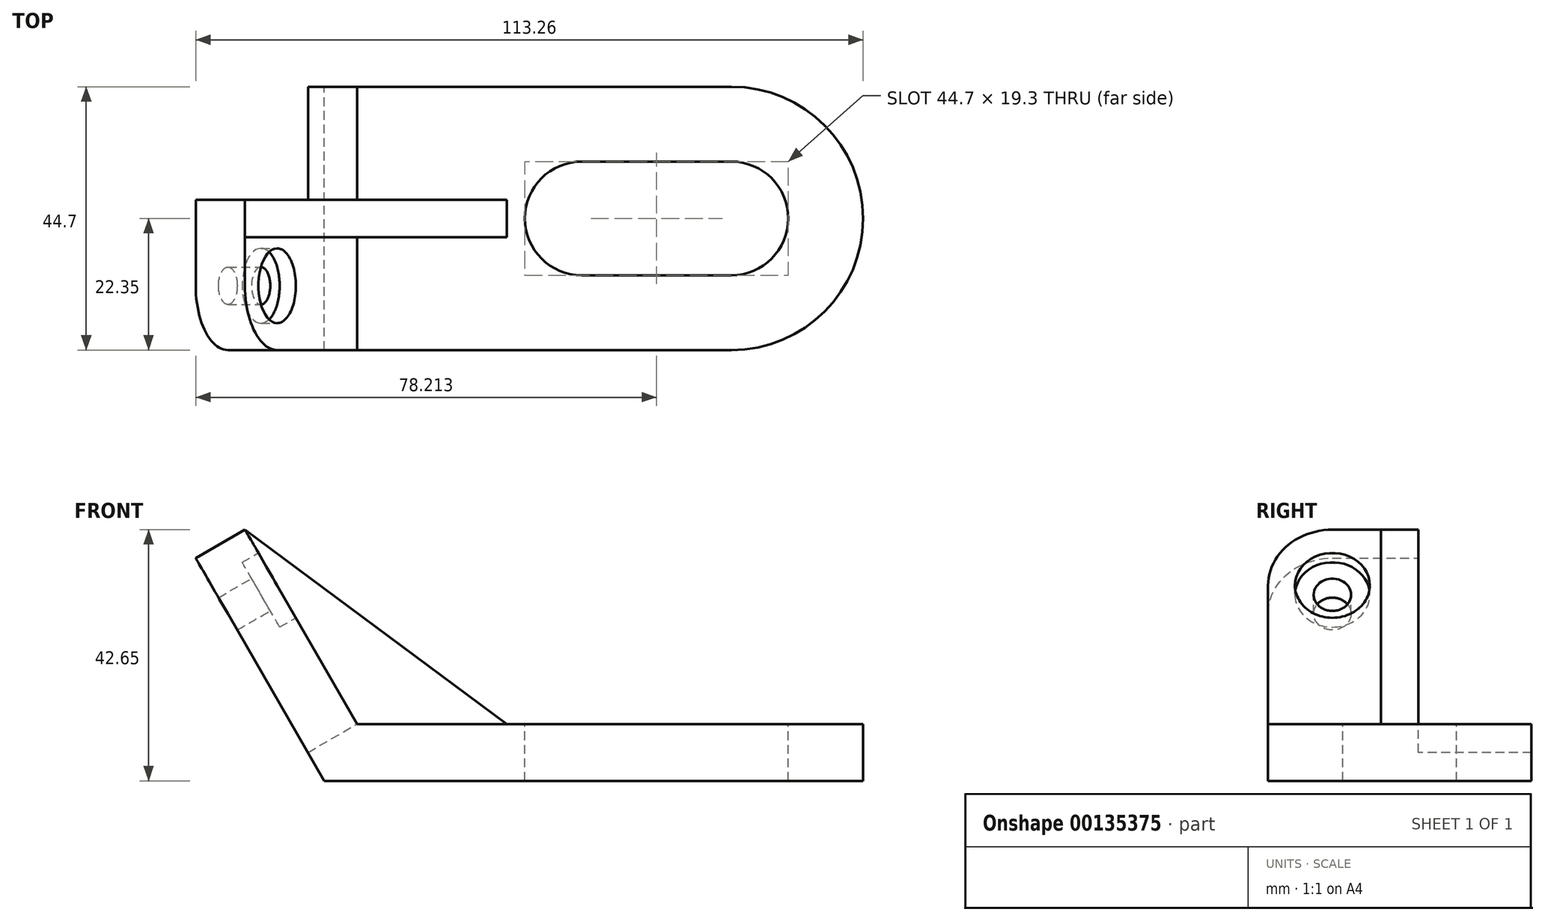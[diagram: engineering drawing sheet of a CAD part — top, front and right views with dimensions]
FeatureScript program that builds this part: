
annotation { "Feature Type Name" : "Feature", "Feature Type Description" : "" }
export const myFeature = defineFeature(function(context is Context, id is Id, definition is map)
    precondition{}
    {
        {
            var Q0;
            Q0=qCreatedBy(makeId("Front.planeOp"),FACE);
            var sketch = newSketch(context, id + "F0", { "sketchPlane" : qUnion([Q0])});
            skLineSegment(sketch, "E0", {"start": v(91.42, 9.65) * mm, "end": v(5.57, 9.65) * mm});
            skLineSegment(sketch, "E1", {"start": v(91.42, 9.65) * mm, "end": v(91.42, 0) * mm});
            skLineSegment(sketch, "E2", {"start": v(91.42, 0) * mm, "end": v(0, 0) * mm});
            skLineSegment(sketch, "E3", {"start": v(0, 0) * mm, "end": v(-21.84, 37.82) * mm});
            skLineSegment(sketch, "E4", {"start": v(-21.84, 37.82) * mm, "end": v(-13.48, 42.65) * mm});
            skLineSegment(sketch, "E5", {"start": v(-13.48, 42.65) * mm, "end": v(5.57, 9.65) * mm});
            skLineSegment(sketch, "E6", {"start": v(-13.48, 42.65) * mm, "end": v(30.97, 9.65) * mm});
            skLineSegment(sketch, "E7", {"start": v(-21.84, 37.82) * mm, "end": v(-21.84, 0) * mm, "construction": true});
            skSolve(sketch);
        }
        {
            var Q0;
            {var subQ0=sQuery(id+"F0.wireOp",EDGE,"E1");Q0=makeQuery(id+"F0.imprint","IMPRINT",FACE,{"disambiguationData":[TD([[makeQuery(id+"F0.imprint","IMPRINT",EDGE,{"derivedFrom":subQ0}),-1.0]])]});}
            extrude(context, id + "F1", {"entities" : qUnion([Q0]), "endBound" : BoundingType.SYMMETRIC, "depth" : 44.7 * mm});
        }
        {
            var Q0;
            {var subQ0=sQuery(id+"F0.wireOp",EDGE,"E5");Q0=makeQuery(id+"F0.imprint","IMPRINT",FACE,{"disambiguationData":[TD([[makeQuery(id+"F0.imprint","IMPRINT",EDGE,{"derivedFrom":subQ0}),1.0]])]});}
            extrude(context, id + "F2", {"entities" : qUnion([Q0]), "operationType" : NewBodyOperationType.ADD, "endBound" : BoundingType.SYMMETRIC, "depth" : 6.35 * mm});
        }
        {
            var Q0;
            Q0=makeQuery(id+"F1.opExtrude","SWEPT_FACE",FACE,{"disambiguationData":[OSD([sQuery(id+"F0.wireOp",EDGE,"E0")])]});
            var sketch = newSketch(context, id + "F3", { "sketchPlane" : qUnion([Q0])});
            skArc(sketch, "E8", {"start": v(43.67, 9.65) * mm, "mid": v(34.02, 0) * mm, "end": v(43.67, -9.65) * mm});
            skArc(sketch, "E9", {"start": v(69.07, -9.65) * mm, "mid": v(78.72, 0) * mm, "end": v(69.07, 9.65) * mm});
            skLineSegment(sketch, "E10", {"start": v(43.67, 9.65) * mm, "end": v(69.07, 9.65) * mm});
            skLineSegment(sketch, "E11", {"start": v(69.07, -9.65) * mm, "end": v(43.67, -9.65) * mm});
            skArc(sketch, "E12", {"start": v(69.07, -22.35) * mm, "mid": v(91.42, 0) * mm, "end": v(69.07, 22.35) * mm});
            skLineSegment(sketch, "E13", {"start": v(69.07, 22.35) * mm, "end": v(69.07, -22.35) * mm});
            skSolve(sketch);
        }
        {
            var Q0;
            Q0=makeQuery(id+"F3.imprint","IMPRINT",FACE,{"disambiguationData":[TD([[makeQuery(id+"F3.imprint","IMPRINT",EDGE,{"derivedFrom":sQuery(id+"F3.wireOp",EDGE,"E8")}),1.0]])]});
            var Q1;
            {var subQ0=sQuery(id+"F3.wireOp",EDGE,"E9");Q1=makeQuery(id+"F3.imprint","IMPRINT",FACE,{"disambiguationData":[TD([[makeQuery(id+"F3.imprint","IMPRINT",EDGE,{"derivedFrom":subQ0}),1.0]])]});}
            var Q2;
            {var subQ0=sQuery(id+"F3.wireOp",EDGE,"E12");var subQ1=sQuery(id+"F0.wireOp",EDGE,"E0");var subQ2=makeQuery(id+"F1.opExtrude","CAP_EDGE",EDGE,{"disambiguationData":[OSD([subQ1])],"isStart":true});var subQ3=makeQuery(id+"F3.imprint","INTERSECT",VERTEX,{"derivedFrom":[subQ2,subQ0,sQuery(id+"F3.wireOp",EDGE,"E13")]});Q2=makeQuery(id+"F3.imprint","IMPRINT",FACE,{"disambiguationData":[TD([[makeQuery(id+"F3.imprint","IMPRINT",EDGE,{"disambiguationData":[TD([[subQ3,1.0]])],"derivedFrom":subQ0}),-1.0]])]});}
            var Q3;
            {var subQ0=sQuery(id+"F3.wireOp",EDGE,"E12");var subQ1=sQuery(id+"F0.wireOp",EDGE,"E0");var subQ2=makeQuery(id+"F1.opExtrude","CAP_EDGE",EDGE,{"disambiguationData":[OSD([subQ1])],"isStart":false});var subQ3=makeQuery(id+"F3.imprint","INTERSECT",VERTEX,{"derivedFrom":[subQ2,subQ0,sQuery(id+"F3.wireOp",EDGE,"E13")]});Q3=makeQuery(id+"F3.imprint","IMPRINT",FACE,{"disambiguationData":[TD([[makeQuery(id+"F3.imprint","IMPRINT",EDGE,{"disambiguationData":[TD([[subQ3,-1.0]])],"derivedFrom":subQ0}),-1.0]])]});}
            extrude(context, id + "F4", {"entities" : qUnion([Q0, Q1, Q2, Q3]), "operationType" : NewBodyOperationType.REMOVE, "oppositeDirection" : true, "depth" : 9.65 * mm});
        }
        {
            var Q0;
            {var subQ0=sQuery(id+"F0.wireOp",EDGE,"E6");var subQ1=sQuery(id+"F0.wireOp",EDGE,"E5");var subQ2=sQuery(id+"F0.wireOp",EDGE,"E0");Q0=makeQuery(id+"F2.boolean.opBoolean","SPLIT",FACE,{"disambiguationData":[TD([makeQuery(id+"F2.opExtrude","CAP_FACE",FACE,{"disambiguationData":[OSD([subQ2,subQ1,subQ0])],"isStart":false})])],"derivedFrom":makeQuery(id+"F1.opExtrude","SWEPT_FACE",FACE,{"disambiguationData":[OSD([subQ1])]})});}
            var Q1;
            {var subQ0=sQuery(id+"F0.wireOp",EDGE,"E6");var subQ1=sQuery(id+"F0.wireOp",EDGE,"E5");var subQ2=sQuery(id+"F0.wireOp",EDGE,"E0");Q1=makeQuery(id+"F2.boolean.opBoolean","SPLIT",FACE,{"disambiguationData":[TD([makeQuery(id+"F2.opExtrude","CAP_FACE",FACE,{"disambiguationData":[OSD([subQ2,subQ1,subQ0])],"isStart":false})])],"derivedFrom":makeQuery(id+"F1.opExtrude","SWEPT_FACE",FACE,{"disambiguationData":[OSD([subQ1])]})});}
            var sketch = newSketch(context, id + "F5", { "sketchPlane" : qUnion([Q0, Q1])});
            skCircle(sketch, "E14", {"center": v(-11.43, 32.75) * mm, "radius": 3.18 * mm});
            skCircle(sketch, "E15", {"center": v(-11.43, 32.75) * mm, "radius": 6.35 * mm});
            skCircle(sketch, "E16.MirrorC", {"center": v(11.43, 32.75) * mm, "radius": 6.35 * mm});
            skCircle(sketch, "E17.MirrorC", {"center": v(11.43, 32.75) * mm, "radius": 3.18 * mm});
            skSolve(sketch);
        }
        {
            var Q0;
            Q0=makeQuery(id+"F5.imprint","IMPRINT",FACE,{"disambiguationData":[TD([[makeQuery(id+"F5.imprint","IMPRINT",EDGE,{"derivedFrom":sQuery(id+"F5.wireOp",EDGE,"E14")}),-1.0]])]});
            var Q1;
            Q1=makeQuery(id+"F5.imprint","IMPRINT",FACE,{"disambiguationData":[TD([[makeQuery(id+"F5.imprint","IMPRINT",EDGE,{"derivedFrom":sQuery(id+"F5.wireOp",EDGE,"E16.MirrorC")}),-1.0]])]});
            extrude(context, id + "F6", {"entities" : qUnion([Q0, Q1]), "operationType" : NewBodyOperationType.REMOVE, "oppositeDirection" : true, "depth" : 3.17 * mm});
        }
        {
            var Q0;
            {var subQ0=sQuery(id+"F0.wireOp",EDGE,"E6");var subQ1=sQuery(id+"F0.wireOp",EDGE,"E5");var subQ2=sQuery(id+"F0.wireOp",EDGE,"E0");Q0=makeQuery(id+"F6.boolean.opBoolean","SPLIT",FACE,{"disambiguationData":[TD([makeQuery(id+"F6.opExtrude","SWEPT_FACE",FACE,{"disambiguationData":[OSD([sQuery(id+"F5.wireOp",EDGE,"E14")])]})])],"derivedFrom":makeQuery(id+"F2.boolean.opBoolean","SPLIT",FACE,{"disambiguationData":[TD([makeQuery(id+"F2.opExtrude","CAP_FACE",FACE,{"disambiguationData":[OSD([subQ2,subQ1,subQ0])],"isStart":false})])],"derivedFrom":makeQuery(id+"F1.opExtrude","SWEPT_FACE",FACE,{"disambiguationData":[OSD([subQ1])]})})});}
            var Q1;
            {var subQ0=sQuery(id+"F0.wireOp",EDGE,"E6");var subQ1=sQuery(id+"F0.wireOp",EDGE,"E5");var subQ2=sQuery(id+"F0.wireOp",EDGE,"E0");Q1=makeQuery(id+"F6.boolean.opBoolean","SPLIT",FACE,{"disambiguationData":[TD([makeQuery(id+"F6.opExtrude","SWEPT_FACE",FACE,{"disambiguationData":[OSD([sQuery(id+"F5.wireOp",EDGE,"E17.MirrorC")])]})])],"derivedFrom":makeQuery(id+"F2.boolean.opBoolean","SPLIT",FACE,{"disambiguationData":[TD([makeQuery(id+"F2.opExtrude","CAP_FACE",FACE,{"disambiguationData":[OSD([subQ2,subQ1,subQ0])],"isStart":true})])],"derivedFrom":makeQuery(id+"F1.opExtrude","SWEPT_FACE",FACE,{"disambiguationData":[OSD([subQ1])]})})});}
            extrude(context, id + "F7", {"entities" : qUnion([Q0, Q1]), "operationType" : NewBodyOperationType.REMOVE, "oppositeDirection" : true, "depth" : 25.4 * mm});
        }
        {
            var Q0;
            Q0=makeQuery(id+"F1.opExtrude","CAP_EDGE",EDGE,{"disambiguationData":[OSD([sQuery(id+"F0.wireOp",EDGE,"E4")])],"isStart":false});
            var Q1;
            Q1=makeQuery(id+"F1.opExtrude","CAP_EDGE",EDGE,{"disambiguationData":[OSD([sQuery(id+"F0.wireOp",EDGE,"E4")])],"isStart":true});
            fillet(context, id + "F8", {"entities" : qUnion([Q0, Q1]), "radius" : 10.92 * mm, "tangentPropagation" : true, "allowEdgeOverflow" : false});
        }
    });
